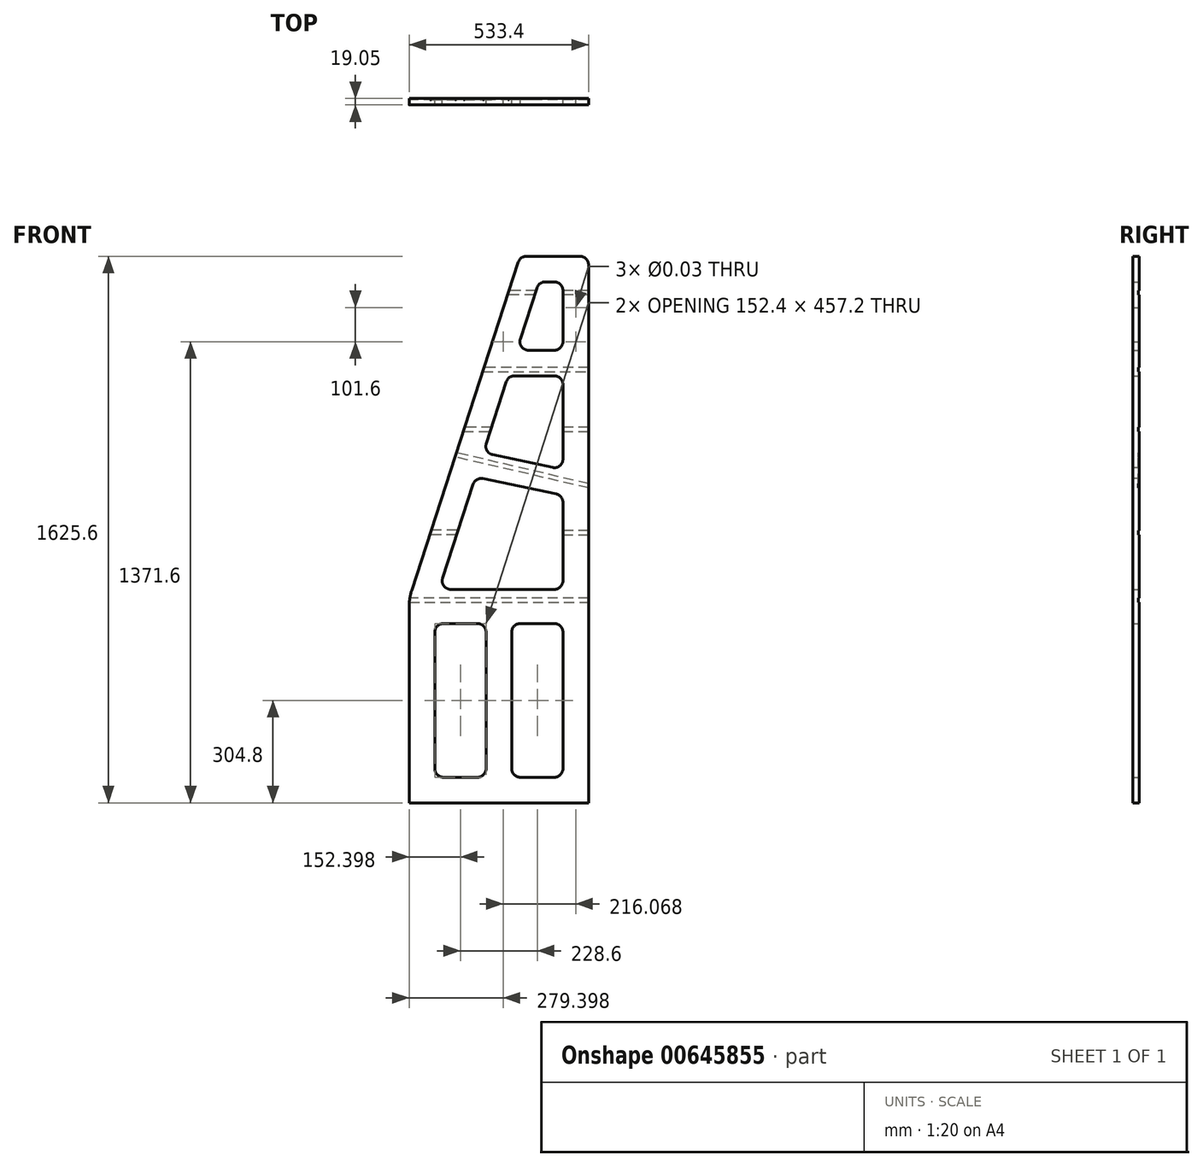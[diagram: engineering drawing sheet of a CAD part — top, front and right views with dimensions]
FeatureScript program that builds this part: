
annotation { "Feature Type Name" : "Feature", "Feature Type Description" : "" }
export const myFeature = defineFeature(function(context is Context, id is Id, definition is map)
    precondition{}
    {
        {
            var Q0;
            Q0=qCreatedBy(makeId("Front.planeOp"),FACE);
            var sketch = newSketch(context, id + "F0", { "sketchPlane" : qUnion([Q0])});
            skLineSegment(sketch, "E0.bottom", {"start": v(223.33, 799.48) * mm, "end": v(20.13, 799.48) * mm});
            skLineSegment(sketch, "E0.top", {"start": v(223.33, -826.12) * mm, "end": v(-310.07, -826.12) * mm});
            skLineSegment(sketch, "E0.left", {"start": v(223.33, 799.48) * mm, "end": v(223.33, -826.12) * mm});
            skLineSegment(sketch, "E0.right", {"start": v(-310.07, -216.52) * mm, "end": v(-310.07, -826.12) * mm});
            skPoint(sketch, "E0.middle", {"position": v(-43.37, -13.32) * mm});
            skLineSegment(sketch, "E1", {"start": v(-310.07, -216.52) * mm, "end": v(20.13, 799.48) * mm});
            skPoint(sketch, "E2.orphan", {"position": v(-310.07, 799.48) * mm});
            skPoint(sketch, "E3", {"position": v(-233.87, -749.92) * mm});
            skPoint(sketch, "E4", {"position": v(147.13, -749.92) * mm});
            skPoint(sketch, "E5", {"position": v(147.13, -292.72) * mm});
            skPoint(sketch, "E6", {"position": v(-5.27, -292.72) * mm});
            skPoint(sketch, "E7", {"position": v(-5.27, -749.92) * mm});
            skPoint(sketch, "E8", {"position": v(-81.47, -292.72) * mm});
            skPoint(sketch, "E9", {"position": v(-81.47, -749.92) * mm});
            skPoint(sketch, "E10", {"position": v(-233.87, -292.72) * mm});
            skPoint(sketch, "E11", {"position": v(-221.7, -191.12) * mm});
            skPoint(sketch, "E12", {"position": v(147.13, -191.12) * mm});
            skPoint(sketch, "E13", {"position": v(147.13, 113.68) * mm});
            skPoint(sketch, "E14", {"position": v(-122.63, 113.68) * mm});
            skPoint(sketch, "E15", {"position": v(147.13, 215.28) * mm});
            skPoint(sketch, "E16", {"position": v(147.13, 723.28) * mm});
            skPoint(sketch, "E17", {"position": v(147.13, 443.88) * mm});
            skLineSegment(sketch, "E18", {"start": v(-233.87, -292.72) * mm, "end": v(-81.47, -292.72) * mm});
            skLineSegment(sketch, "E19", {"start": v(-81.47, -749.92) * mm, "end": v(-233.87, -749.92) * mm});
            skLineSegment(sketch, "E20", {"start": v(-233.87, -292.72) * mm, "end": v(-233.87, -749.92) * mm});
            skLineSegment(sketch, "E21", {"start": v(-81.47, -749.92) * mm, "end": v(-81.47, -292.72) * mm});
            skLineSegment(sketch, "E22", {"start": v(-5.27, -292.72) * mm, "end": v(-5.27, -749.92) * mm});
            skLineSegment(sketch, "E23", {"start": v(-5.27, -749.92) * mm, "end": v(147.13, -749.92) * mm});
            skLineSegment(sketch, "E24", {"start": v(147.13, -749.92) * mm, "end": v(147.13, -292.72) * mm});
            skLineSegment(sketch, "E25", {"start": v(-5.27, -292.72) * mm, "end": v(147.13, -292.72) * mm});
            skLineSegment(sketch, "E26", {"start": v(-221.7, -191.12) * mm, "end": v(-122.63, 113.68) * mm});
            skLineSegment(sketch, "E27", {"start": v(-221.7, -191.12) * mm, "end": v(147.13, -191.12) * mm});
            skLineSegment(sketch, "E28", {"start": v(147.13, -191.12) * mm, "end": v(147.13, 113.68) * mm});
            skPoint(sketch, "E29", {"position": v(-89.61, 215.28) * mm});
            skLineSegment(sketch, "E30", {"start": v(147.13, 215.28) * mm, "end": v(147.13, 443.88) * mm});
            skPoint(sketch, "E31", {"position": v(-15.32, 443.88) * mm});
            skPoint(sketch, "E32", {"position": v(147.13, 520.08) * mm});
            skPoint(sketch, "E33", {"position": v(9.45, 520.08) * mm});
            skLineSegment(sketch, "E34", {"start": v(-15.32, 443.88) * mm, "end": v(147.13, 443.88) * mm});
            skLineSegment(sketch, "E35", {"start": v(-15.32, 443.88) * mm, "end": v(-89.61, 215.28) * mm});
            skLineSegment(sketch, "E36", {"start": v(147.13, 723.28) * mm, "end": v(147.13, 520.08) * mm});
            skLineSegment(sketch, "E37", {"start": v(147.13, 520.08) * mm, "end": v(9.45, 520.08) * mm});
            skLineSegment(sketch, "E38", {"start": v(147.13, 723.28) * mm, "end": v(75.3, 723.28) * mm});
            skLineSegment(sketch, "E39", {"start": v(9.45, 520.08) * mm, "end": v(75.3, 723.28) * mm});
            skPoint(sketch, "E40", {"position": v(147.13, 88.28) * mm});
            skPoint(sketch, "E41", {"position": v(147.13, 164.48) * mm});
            skLineSegment(sketch, "E42", {"start": v(-89.61, 215.28) * mm, "end": v(147.13, 164.48) * mm});
            skLineSegment(sketch, "E43", {"start": v(147.13, 164.48) * mm, "end": v(147.13, 215.28) * mm});
            skPoint(sketch, "E44", {"position": v(-113.17, 142.81) * mm});
            skLineSegment(sketch, "E45", {"start": v(-113.17, 142.81) * mm, "end": v(147.13, 88.28) * mm});
            skLineSegment(sketch, "E46", {"start": v(-122.63, 113.68) * mm, "end": v(-113.17, 142.81) * mm});
            skSolve(sketch);
        }
        {
            var Q0;
            Q0=makeQuery(id+"F0.imprint","IMPRINT",FACE,{"disambiguationData":[TD([[makeQuery(id+"F0.imprint","IMPRINT",EDGE,{"derivedFrom":sQuery(id+"F0.wireOp",EDGE,"E0.bottom")}),1.0]])]});
            extrude(context, id + "F1", {"entities" : qUnion([Q0]), "depth" : 19.05 * mm, "offsetDistance" : 25 * mm});
        }
        {
            var Q0;
            Q0=makeQuery(id+"F1.opExtrude","SWEPT_EDGE",EDGE,{"disambiguationData":[OSD([sQuery(id+"F0.wireOp",EDGE,"E19"),sQuery(id+"F0.wireOp",EDGE,"E20")])]});
            var Q1;
            Q1=makeQuery(id+"F1.opExtrude","SWEPT_EDGE",EDGE,{"disambiguationData":[OSD([sQuery(id+"F0.wireOp",EDGE,"E26"),sQuery(id+"F0.wireOp",EDGE,"E27")])]});
            var Q2;
            Q2=makeQuery(id+"F1.opExtrude","SWEPT_EDGE",EDGE,{"disambiguationData":[OSD([sQuery(id+"F0.wireOp",EDGE,"E35"),sQuery(id+"F0.wireOp",EDGE,"E42")])]});
            var Q3;
            Q3=makeQuery(id+"F1.opExtrude","SWEPT_EDGE",EDGE,{"disambiguationData":[OSD([sQuery(id+"F0.wireOp",EDGE,"E37"),sQuery(id+"F0.wireOp",EDGE,"E39")])]});
            var Q4;
            Q4=makeQuery(id+"F1.opExtrude","SWEPT_EDGE",EDGE,{"disambiguationData":[OSD([sQuery(id+"F0.wireOp",EDGE,"E36"),sQuery(id+"F0.wireOp",EDGE,"E37")])]});
            var Q5;
            Q5=makeQuery(id+"F1.opExtrude","SWEPT_EDGE",EDGE,{"disambiguationData":[OSD([sQuery(id+"F0.wireOp",EDGE,"E42"),sQuery(id+"F0.wireOp",EDGE,"E43")])]});
            var Q6;
            Q6=makeQuery(id+"F1.opExtrude","SWEPT_EDGE",EDGE,{"disambiguationData":[OSD([sQuery(id+"F0.wireOp",EDGE,"E27"),sQuery(id+"F0.wireOp",EDGE,"E28")])]});
            var Q7;
            Q7=makeQuery(id+"F1.opExtrude","SWEPT_EDGE",EDGE,{"disambiguationData":[OSD([sQuery(id+"F0.wireOp",EDGE,"E23"),sQuery(id+"F0.wireOp",EDGE,"E24")])]});
            var Q8;
            Q8=makeQuery(id+"F1.opExtrude","SWEPT_EDGE",EDGE,{"disambiguationData":[OSD([sQuery(id+"F0.wireOp",EDGE,"E19"),sQuery(id+"F0.wireOp",EDGE,"E21")])]});
            var Q9;
            Q9=makeQuery(id+"F1.opExtrude","SWEPT_EDGE",EDGE,{"disambiguationData":[OSD([sQuery(id+"F0.wireOp",EDGE,"E22"),sQuery(id+"F0.wireOp",EDGE,"E23")])]});
            var Q10;
            Q10=makeQuery(id+"F1.opExtrude","SWEPT_EDGE",EDGE,{"disambiguationData":[OSD([sQuery(id+"F0.wireOp",EDGE,"E24"),sQuery(id+"F0.wireOp",EDGE,"E25")])]});
            var Q11;
            Q11=makeQuery(id+"F1.opExtrude","SWEPT_EDGE",EDGE,{"disambiguationData":[OSD([sQuery(id+"F0.wireOp",EDGE,"E22"),sQuery(id+"F0.wireOp",EDGE,"E25")])]});
            var Q12;
            Q12=makeQuery(id+"F1.opExtrude","SWEPT_EDGE",EDGE,{"disambiguationData":[OSD([sQuery(id+"F0.wireOp",EDGE,"E18"),sQuery(id+"F0.wireOp",EDGE,"E20")])]});
            var Q13;
            Q13=makeQuery(id+"F1.opExtrude","SWEPT_EDGE",EDGE,{"disambiguationData":[OSD([sQuery(id+"F0.wireOp",EDGE,"E18"),sQuery(id+"F0.wireOp",EDGE,"E21")])]});
            var Q14;
            Q14=makeQuery(id+"F1.opExtrude","SWEPT_EDGE",EDGE,{"disambiguationData":[OSD([sQuery(id+"F0.wireOp",EDGE,"E28"),sQuery(id+"F0.wireOp",EDGE,"E45")])]});
            var Q15;
            Q15=makeQuery(id+"F1.opExtrude","SWEPT_EDGE",EDGE,{"disambiguationData":[OSD([sQuery(id+"F0.wireOp",EDGE,"E30"),sQuery(id+"F0.wireOp",EDGE,"E34")])]});
            var Q16;
            Q16=makeQuery(id+"F1.opExtrude","SWEPT_EDGE",EDGE,{"disambiguationData":[OSD([sQuery(id+"F0.wireOp",EDGE,"E36"),sQuery(id+"F0.wireOp",EDGE,"E38")])]});
            var Q17;
            Q17=makeQuery(id+"F1.opExtrude","SWEPT_EDGE",EDGE,{"disambiguationData":[OSD([sQuery(id+"F0.wireOp",EDGE,"E34"),sQuery(id+"F0.wireOp",EDGE,"E35")])]});
            var Q18;
            Q18=makeQuery(id+"F1.opExtrude","SWEPT_EDGE",EDGE,{"disambiguationData":[OSD([sQuery(id+"F0.wireOp",EDGE,"E38"),sQuery(id+"F0.wireOp",EDGE,"E39")])]});
            var Q19;
            Q19=makeQuery(id+"F1.opExtrude","SWEPT_EDGE",EDGE,{"disambiguationData":[OSD([sQuery(id+"F0.wireOp",EDGE,"E45"),sQuery(id+"F0.wireOp",EDGE,"E46")])]});
            var Q20;
            Q20=makeQuery(id+"F1.opExtrude","SWEPT_EDGE",EDGE,{"disambiguationData":[OSD([sQuery(id+"F0.wireOp",EDGE,"E0.bottom"),sQuery(id+"F0.wireOp",EDGE,"E0.left")])]});
            var Q21;
            Q21=makeQuery(id+"F1.opExtrude","SWEPT_EDGE",EDGE,{"disambiguationData":[OSD([sQuery(id+"F0.wireOp",EDGE,"E0.bottom"),sQuery(id+"F0.wireOp",EDGE,"E1")])]});
            fillet(context, id + "F2", {"entities" : qUnion([Q0, Q1, Q2, Q3, Q4, Q5, Q6, Q7, Q8, Q9, Q10, Q11, Q12, Q13, Q14, Q15, Q16, Q17, Q18, Q19, Q20, Q21]), "radius" : 25.4 * mm, "tangentPropagation" : true, "allowEdgeOverflow" : false});
        }
        {
            var Q0;
            Q0=makeQuery(id+"F1.opExtrude","SWEPT_EDGE",EDGE,{"disambiguationData":[OSD([sQuery(id+"F0.wireOp",EDGE,"E0.right"),sQuery(id+"F0.wireOp",EDGE,"E1")])]});
            fillet(context, id + "F3", {"entities" : qUnion([Q0]), "radius" : 152.4 * mm, "tangentPropagation" : true, "allowEdgeOverflow" : false});
        }
        {
            var Q0;
            Q0=makeQuery(id+"F1.opExtrude","CAP_FACE",FACE,{"disambiguationData":[OSD([sQuery(id+"F0.wireOp",EDGE,"E0.bottom"),sQuery(id+"F0.wireOp",EDGE,"E0.top"),sQuery(id+"F0.wireOp",EDGE,"E0.left"),sQuery(id+"F0.wireOp",EDGE,"E0.right"),sQuery(id+"F0.wireOp",EDGE,"E1"),sQuery(id+"F0.wireOp",EDGE,"E18"),sQuery(id+"F0.wireOp",EDGE,"E19"),sQuery(id+"F0.wireOp",EDGE,"E20"),sQuery(id+"F0.wireOp",EDGE,"E21"),sQuery(id+"F0.wireOp",EDGE,"E22"),sQuery(id+"F0.wireOp",EDGE,"E23"),sQuery(id+"F0.wireOp",EDGE,"E24"),sQuery(id+"F0.wireOp",EDGE,"E25"),sQuery(id+"F0.wireOp",EDGE,"E26"),sQuery(id+"F0.wireOp",EDGE,"E27"),sQuery(id+"F0.wireOp",EDGE,"E28"),sQuery(id+"F0.wireOp",EDGE,"E30"),sQuery(id+"F0.wireOp",EDGE,"E34"),sQuery(id+"F0.wireOp",EDGE,"E35"),sQuery(id+"F0.wireOp",EDGE,"E36"),sQuery(id+"F0.wireOp",EDGE,"E37"),sQuery(id+"F0.wireOp",EDGE,"E38"),sQuery(id+"F0.wireOp",EDGE,"E39"),sQuery(id+"F0.wireOp",EDGE,"E42"),sQuery(id+"F0.wireOp",EDGE,"E43"),sQuery(id+"F0.wireOp",EDGE,"E45"),sQuery(id+"F0.wireOp",EDGE,"E46")])],"isStart":true});
            var sketch = newSketch(context, id + "F4", { "sketchPlane" : qUnion([Q0])});
            skPoint(sketch, "E47", {"position": v(169.74, 215.28) * mm});
            skPoint(sketch, "E48", {"position": v(-223.33, 123.2) * mm});
            skPoint(sketch, "E49", {"position": v(173.86, 202.58) * mm});
            skPoint(sketch, "E50", {"position": v(-223.33, 110.5) * mm});
            skLineSegment(sketch, "E51", {"start": v(-223.33, 123.2) * mm, "end": v(169.74, 215.28) * mm});
            skLineSegment(sketch, "E52", {"start": v(-223.33, 110.5) * mm, "end": v(173.86, 202.58) * mm});
            skLineSegment(sketch, "E53", {"start": v(-223.33, 123.2) * mm, "end": v(-223.33, 110.5) * mm});
            skLineSegment(sketch, "E54", {"start": v(169.74, 215.28) * mm, "end": v(173.86, 202.58) * mm});
            skSolve(sketch);
        }
        {
            var Q0;
            Q0=makeQuery(id+"F4.imprint","IMPRINT",FACE,{"disambiguationData":[TD([[makeQuery(id+"F4.imprint","IMPRINT",EDGE,{"derivedFrom":sQuery(id+"F4.wireOp",EDGE,"E51")}),-1.0]])]});
            extrude(context, id + "F5", {"entities" : qUnion([Q0]), "operationType" : NewBodyOperationType.REMOVE, "oppositeDirection" : true, "depth" : 3.17 * mm, "offsetDistance" : 25.4 * mm});
        }
        {
            var Q0;
            {var subQ0=sQuery(id+"F0.wireOp",EDGE,"E28");var subQ1=sQuery(id+"F0.wireOp",EDGE,"E23");var subQ2=sQuery(id+"F0.wireOp",EDGE,"E22");var subQ3=sQuery(id+"F0.wireOp",EDGE,"E27");var subQ4=sQuery(id+"F0.wireOp",EDGE,"E25");var subQ5=sQuery(id+"F0.wireOp",EDGE,"E46");var subQ6=sQuery(id+"F0.wireOp",EDGE,"E26");var subQ7=sQuery(id+"F0.wireOp",EDGE,"E20");var subQ8=sQuery(id+"F0.wireOp",EDGE,"E19");var subQ9=sQuery(id+"F0.wireOp",EDGE,"E21");var subQ10=sQuery(id+"F0.wireOp",EDGE,"E24");var subQ11=sQuery(id+"F0.wireOp",EDGE,"E1");var subQ12=sQuery(id+"F0.wireOp",EDGE,"E0.right");var subQ13=sQuery(id+"F0.wireOp",EDGE,"E0.left");var subQ14=sQuery(id+"F0.wireOp",EDGE,"E45");var subQ15=sQuery(id+"F0.wireOp",EDGE,"E0.top");var subQ16=sQuery(id+"F0.wireOp",EDGE,"E18");Q0=makeQuery(id+"F5.boolean.opBoolean","SPLIT",FACE,{"disambiguationData":[TD([makeQuery(id+"F1.opExtrude","SWEPT_FACE",FACE,{"disambiguationData":[OSD([subQ15])]})])],"derivedFrom":makeQuery(id+"F1.opExtrude","CAP_FACE",FACE,{"disambiguationData":[OSD([sQuery(id+"F0.wireOp",EDGE,"E0.bottom"),subQ15,subQ13,subQ12,subQ11,subQ16,subQ8,subQ7,subQ9,subQ2,subQ1,subQ10,subQ4,subQ6,subQ3,subQ0,sQuery(id+"F0.wireOp",EDGE,"E30"),sQuery(id+"F0.wireOp",EDGE,"E34"),sQuery(id+"F0.wireOp",EDGE,"E35"),sQuery(id+"F0.wireOp",EDGE,"E36"),sQuery(id+"F0.wireOp",EDGE,"E37"),sQuery(id+"F0.wireOp",EDGE,"E38"),sQuery(id+"F0.wireOp",EDGE,"E39"),sQuery(id+"F0.wireOp",EDGE,"E42"),sQuery(id+"F0.wireOp",EDGE,"E43"),subQ14,subQ5])],"isStart":true})});}
            var sketch = newSketch(context, id + "F6", { "sketchPlane" : qUnion([Q0])});
            skPoint(sketch, "E55", {"position": v(-223.33, -16.5) * mm});
            skPoint(sketch, "E56", {"position": v(-223.33, -29.2) * mm});
            skLineSegment(sketch, "E57", {"start": v(-223.33, -16.5) * mm, "end": v(-147.13, -16.5) * mm});
            skLineSegment(sketch, "E58", {"start": v(-147.13, -16.5) * mm, "end": v(-147.13, -29.2) * mm});
            skLineSegment(sketch, "E59", {"start": v(-147.13, -29.2) * mm, "end": v(-223.33, -29.2) * mm});
            skSolve(sketch);
        }
        {
            var Q0;
            Q0 = qSketchRegion(id + "F6", true);
            var Q1;
            {var subQ0=sQuery(id+"F6.wireOp",EDGE,"E57");Q1=makeQuery(id+"F6.imprint","IMPRINT",FACE,{"disambiguationData":[TD([[makeQuery(id+"F6.imprint","IMPRINT",EDGE,{"derivedFrom":subQ0}),-1.0]])]});}
            extrude(context, id + "F7", {"entities" : qUnion([Q0, Q1]), "operationType" : NewBodyOperationType.REMOVE, "oppositeDirection" : true, "depth" : 3.17 * mm, "offsetDistance" : 25.4 * mm});
        }
        {
            var Q0;
            {var subQ0=sQuery(id+"F0.wireOp",EDGE,"E39");var subQ1=sQuery(id+"F0.wireOp",EDGE,"E38");var subQ2=sQuery(id+"F0.wireOp",EDGE,"E36");var subQ3=sQuery(id+"F0.wireOp",EDGE,"E0.bottom");var subQ4=sQuery(id+"F0.wireOp",EDGE,"E42");var subQ5=sQuery(id+"F0.wireOp",EDGE,"E35");var subQ6=sQuery(id+"F0.wireOp",EDGE,"E34");var subQ7=sQuery(id+"F0.wireOp",EDGE,"E30");var subQ8=sQuery(id+"F0.wireOp",EDGE,"E37");var subQ9=sQuery(id+"F0.wireOp",EDGE,"E0.left");var subQ10=sQuery(id+"F0.wireOp",EDGE,"E1");var subQ11=sQuery(id+"F0.wireOp",EDGE,"E43");Q0=makeQuery(id+"F5.boolean.opBoolean","SPLIT",FACE,{"disambiguationData":[TD([makeQuery(id+"F1.opExtrude","SWEPT_FACE",FACE,{"disambiguationData":[OSD([subQ3])]})])],"derivedFrom":makeQuery(id+"F1.opExtrude","CAP_FACE",FACE,{"disambiguationData":[OSD([subQ3,sQuery(id+"F0.wireOp",EDGE,"E0.top"),subQ9,sQuery(id+"F0.wireOp",EDGE,"E0.right"),subQ10,sQuery(id+"F0.wireOp",EDGE,"E18"),sQuery(id+"F0.wireOp",EDGE,"E19"),sQuery(id+"F0.wireOp",EDGE,"E20"),sQuery(id+"F0.wireOp",EDGE,"E21"),sQuery(id+"F0.wireOp",EDGE,"E22"),sQuery(id+"F0.wireOp",EDGE,"E23"),sQuery(id+"F0.wireOp",EDGE,"E24"),sQuery(id+"F0.wireOp",EDGE,"E25"),sQuery(id+"F0.wireOp",EDGE,"E26"),sQuery(id+"F0.wireOp",EDGE,"E27"),sQuery(id+"F0.wireOp",EDGE,"E28"),subQ7,subQ6,subQ5,subQ2,subQ8,subQ1,subQ0,subQ4,subQ11,sQuery(id+"F0.wireOp",EDGE,"E45"),sQuery(id+"F0.wireOp",EDGE,"E46")])],"isStart":true})});}
            var sketch = newSketch(context, id + "F8", { "sketchPlane" : qUnion([Q0])});
            skPoint(sketch, "E60", {"position": v(-223.33, 685.18) * mm});
            skPoint(sketch, "E61", {"position": v(-223.33, 697.88) * mm});
            skLineSegment(sketch, "E62", {"start": v(-223.33, 697.88) * mm, "end": v(12.9, 697.88) * mm});
            skLineSegment(sketch, "E63", {"start": v(-223.33, 685.18) * mm, "end": v(-223.33, 697.88) * mm});
            skLineSegment(sketch, "E64", {"start": v(-223.33, 685.18) * mm, "end": v(50.2, 685.18) * mm});
            skLineSegment(sketch, "E65", {"start": v(50.2, 685.18) * mm, "end": v(12.9, 697.88) * mm});
            skSolve(sketch);
        }
        {
            var Q0;
            {var subQ8=sQuery(id+"F8.wireOp",EDGE,"E63");Q0=makeQuery(id+"F8.imprint","IMPRINT",FACE,{"disambiguationData":[TD([[makeQuery(id+"F8.imprint","IMPRINT",EDGE,{"derivedFrom":subQ8}),1.0]])]});}
            var Q1;
            {var subQ0=sQuery(id+"F8.wireOp",EDGE,"gvT0msbo-aJb6-UwI5-asTA-rgO9hPE7J7Gs");Q1=makeQuery(id+"F8.imprint","IMPRINT",FACE,{"disambiguationData":[TD([[makeQuery(id+"F8.imprint","IMPRINT",EDGE,{"derivedFrom":subQ0}),1.0]])]});}
            extrude(context, id + "F9", {"entities" : qUnion([Q0, Q1]), "operationType" : NewBodyOperationType.REMOVE, "oppositeDirection" : true, "depth" : 3.17 * mm, "offsetDistance" : 25.4 * mm});
        }
        {
            var Q0;
            {var subQ0=sQuery(id+"F0.wireOp",EDGE,"E39");var subQ1=sQuery(id+"F0.wireOp",EDGE,"E38");var subQ2=sQuery(id+"F0.wireOp",EDGE,"E36");var subQ3=sQuery(id+"F0.wireOp",EDGE,"E0.bottom");var subQ4=sQuery(id+"F0.wireOp",EDGE,"E42");var subQ5=sQuery(id+"F0.wireOp",EDGE,"E35");var subQ6=sQuery(id+"F0.wireOp",EDGE,"E34");var subQ7=sQuery(id+"F0.wireOp",EDGE,"E30");var subQ8=sQuery(id+"F0.wireOp",EDGE,"E37");var subQ9=sQuery(id+"F0.wireOp",EDGE,"E0.left");var subQ10=sQuery(id+"F0.wireOp",EDGE,"E1");var subQ11=sQuery(id+"F0.wireOp",EDGE,"E43");Q0=makeQuery(id+"F5.boolean.opBoolean","SPLIT",FACE,{"disambiguationData":[TD([makeQuery(id+"F1.opExtrude","SWEPT_FACE",FACE,{"disambiguationData":[OSD([subQ3])]})])],"derivedFrom":makeQuery(id+"F1.opExtrude","CAP_FACE",FACE,{"disambiguationData":[OSD([subQ3,sQuery(id+"F0.wireOp",EDGE,"E0.top"),subQ9,sQuery(id+"F0.wireOp",EDGE,"E0.right"),subQ10,sQuery(id+"F0.wireOp",EDGE,"E18"),sQuery(id+"F0.wireOp",EDGE,"E19"),sQuery(id+"F0.wireOp",EDGE,"E20"),sQuery(id+"F0.wireOp",EDGE,"E21"),sQuery(id+"F0.wireOp",EDGE,"E22"),sQuery(id+"F0.wireOp",EDGE,"E23"),sQuery(id+"F0.wireOp",EDGE,"E24"),sQuery(id+"F0.wireOp",EDGE,"E25"),sQuery(id+"F0.wireOp",EDGE,"E26"),sQuery(id+"F0.wireOp",EDGE,"E27"),sQuery(id+"F0.wireOp",EDGE,"E28"),subQ7,subQ6,subQ5,subQ2,subQ8,subQ1,subQ0,subQ4,subQ11,sQuery(id+"F0.wireOp",EDGE,"E45"),sQuery(id+"F0.wireOp",EDGE,"E46")])],"isStart":true})});}
            var sketch = newSketch(context, id + "F10", { "sketchPlane" : qUnion([Q0])});
            skLineSegment(sketch, "E66", {"start": v(-171.29, 697.88) * mm, "end": v(12.9, 697.88) * mm});
            skLineSegment(sketch, "E67", {"start": v(12.9, 697.88) * mm, "end": v(16.04, 688.18) * mm});
            skLineSegment(sketch, "E68", {"start": v(16.04, 688.18) * mm, "end": v(17.02, 685.18) * mm});
            skLineSegment(sketch, "E69", {"start": v(17.02, 685.18) * mm, "end": v(-220.33, 685.18) * mm});
            skLineSegment(sketch, "E70", {"start": v(-220.33, 685.18) * mm, "end": v(-220.33, 697.88) * mm});
            skLineSegment(sketch, "E71", {"start": v(-220.33, 697.88) * mm, "end": v(-165.3, 697.88) * mm});
            skSolve(sketch);
        }
        {
            var Q0;
            {var subQ11=sQuery(id+"F10.wireOp",EDGE,"E70");Q0=makeQuery(id+"F10.imprint","IMPRINT",FACE,{"disambiguationData":[TD([[makeQuery(id+"F10.imprint","IMPRINT",EDGE,{"derivedFrom":subQ11}),-1.0]])]});}
            var Q1;
            {var subQ5=sQuery(id+"F10.wireOp",EDGE,"E67");Q1=makeQuery(id+"F10.imprint","IMPRINT",FACE,{"disambiguationData":[TD([[makeQuery(id+"F10.imprint","IMPRINT",EDGE,{"derivedFrom":subQ5}),1.0]])]});}
            extrude(context, id + "F11", {"entities" : qUnion([Q0, Q1]), "operationType" : NewBodyOperationType.REMOVE, "oppositeDirection" : true, "depth" : 3.17 * mm, "offsetDistance" : 25.4 * mm});
        }
        {
            var Q0;
            {var subQ0=sQuery(id+"F0.wireOp",EDGE,"E34");var subQ1=sQuery(id+"F0.wireOp",EDGE,"E30");var subQ3=sQuery(id+"F0.wireOp",EDGE,"E36");var subQ5=sQuery(id+"F0.wireOp",EDGE,"E42");var subQ7=sQuery(id+"F0.wireOp",EDGE,"E37");var subQ9=sQuery(id+"F0.wireOp",EDGE,"E39");var subQ12=sQuery(id+"F0.wireOp",EDGE,"E35");var subQ15=sQuery(id+"F0.wireOp",EDGE,"E0.left");var subQ17=makeQuery(id+"F1.opExtrude","SWEPT_FACE",FACE,{"disambiguationData":[OSD([subQ0])]});var subQ18=sQuery(id+"F0.wireOp",EDGE,"E1");var subQ20=sQuery(id+"F0.wireOp",EDGE,"E43");var subQ26=sQuery(id+"F0.wireOp",EDGE,"E38");var subQ27=sQuery(id+"F0.wireOp",EDGE,"E0.bottom");Q0=makeQuery(id+"F11.boolean.opBoolean","SPLIT",FACE,{"disambiguationData":[TD([subQ17])],"derivedFrom":makeQuery(id+"F5.boolean.opBoolean","SPLIT",FACE,{"disambiguationData":[TD([makeQuery(id+"F1.opExtrude","SWEPT_FACE",FACE,{"disambiguationData":[OSD([subQ27])]})])],"derivedFrom":makeQuery(id+"F1.opExtrude","CAP_FACE",FACE,{"disambiguationData":[OSD([subQ27,sQuery(id+"F0.wireOp",EDGE,"E0.top"),subQ15,sQuery(id+"F0.wireOp",EDGE,"E0.right"),subQ18,sQuery(id+"F0.wireOp",EDGE,"E18"),sQuery(id+"F0.wireOp",EDGE,"E19"),sQuery(id+"F0.wireOp",EDGE,"E20"),sQuery(id+"F0.wireOp",EDGE,"E21"),sQuery(id+"F0.wireOp",EDGE,"E22"),sQuery(id+"F0.wireOp",EDGE,"E23"),sQuery(id+"F0.wireOp",EDGE,"E24"),sQuery(id+"F0.wireOp",EDGE,"E25"),sQuery(id+"F0.wireOp",EDGE,"E26"),sQuery(id+"F0.wireOp",EDGE,"E27"),sQuery(id+"F0.wireOp",EDGE,"E28"),subQ1,subQ0,subQ12,subQ3,subQ7,subQ26,subQ9,subQ5,subQ20,sQuery(id+"F0.wireOp",EDGE,"E45"),sQuery(id+"F0.wireOp",EDGE,"E46")])],"isStart":true})})});}
            var sketch = newSketch(context, id + "F12", { "sketchPlane" : qUnion([Q0])});
            skPoint(sketch, "E72", {"position": v(-223.33, 469.28) * mm});
            skPoint(sketch, "E73", {"position": v(-223.33, 456.58) * mm});
            skPoint(sketch, "E74", {"position": v(-223.33, 291.48) * mm});
            skPoint(sketch, "E75", {"position": v(-223.33, 278.78) * mm});
            skLineSegment(sketch, "E76", {"start": v(-223.33, 469.28) * mm, "end": v(87.19, 469.28) * mm});
            skLineSegment(sketch, "E77", {"start": v(87.19, 469.28) * mm, "end": v(91.31, 456.58) * mm});
            skLineSegment(sketch, "E78", {"start": v(91.31, 456.58) * mm, "end": v(-223.33, 456.58) * mm});
            skLineSegment(sketch, "E79", {"start": v(-223.33, 469.28) * mm, "end": v(-223.33, 456.58) * mm});
            skLineSegment(sketch, "E80", {"start": v(-223.33, 291.48) * mm, "end": v(144.97, 291.48) * mm});
            skLineSegment(sketch, "E81", {"start": v(144.97, 291.48) * mm, "end": v(169.74, 278.78) * mm});
            skLineSegment(sketch, "E82", {"start": v(169.74, 278.78) * mm, "end": v(-223.33, 278.78) * mm});
            skLineSegment(sketch, "E83", {"start": v(-223.33, 291.48) * mm, "end": v(-223.33, 278.78) * mm});
            skPoint(sketch, "E84", {"position": v(-185.4, 647.08) * mm});
            skPoint(sketch, "E85", {"position": v(-185.4, 545.48) * mm});
            skSolve(sketch);
        }
        {
            var Q0;
            Q0 = qSketchRegion(id + "F12", true);
            extrude(context, id + "F13", {"entities" : qUnion([Q0]), "operationType" : NewBodyOperationType.REMOVE, "oppositeDirection" : true, "depth" : 3.17 * mm, "offsetDistance" : 25.4 * mm});
        }
        {
            var Q0;
            Q0=sQuery(id+"F12.wireOp",VERTEX,"E84");
            var Q1;
            Q1=sQuery(id+"F12.wireOp",VERTEX,"E85");
            var Q2;
            Q2=makeQuery(id+"F1.opExtrude","SWEPT_BODY",BODY,{"disambiguationData":[OSD([sQuery(id+"F0.wireOp",EDGE,"E0.bottom"),sQuery(id+"F0.wireOp",EDGE,"E0.top"),sQuery(id+"F0.wireOp",EDGE,"E0.left"),sQuery(id+"F0.wireOp",EDGE,"E0.right"),sQuery(id+"F0.wireOp",EDGE,"E1"),sQuery(id+"F0.wireOp",EDGE,"E18"),sQuery(id+"F0.wireOp",EDGE,"E19"),sQuery(id+"F0.wireOp",EDGE,"E20"),sQuery(id+"F0.wireOp",EDGE,"E21"),sQuery(id+"F0.wireOp",EDGE,"E22"),sQuery(id+"F0.wireOp",EDGE,"E23"),sQuery(id+"F0.wireOp",EDGE,"E24"),sQuery(id+"F0.wireOp",EDGE,"E25"),sQuery(id+"F0.wireOp",EDGE,"E26"),sQuery(id+"F0.wireOp",EDGE,"E27"),sQuery(id+"F0.wireOp",EDGE,"E28"),sQuery(id+"F0.wireOp",EDGE,"E30"),sQuery(id+"F0.wireOp",EDGE,"E34"),sQuery(id+"F0.wireOp",EDGE,"E35"),sQuery(id+"F0.wireOp",EDGE,"E36"),sQuery(id+"F0.wireOp",EDGE,"E37"),sQuery(id+"F0.wireOp",EDGE,"E38"),sQuery(id+"F0.wireOp",EDGE,"E39"),sQuery(id+"F0.wireOp",EDGE,"E42"),sQuery(id+"F0.wireOp",EDGE,"E43"),sQuery(id+"F0.wireOp",EDGE,"E45"),sQuery(id+"F0.wireOp",EDGE,"E46")])]});
            hole(context, id + "F14", {"style" : HoleStyle.SIMPLE, "endStyle" : HoleEndStyle.THROUGH, "standardTappedOrClearance" : lookupTablePath({ "standard" : "ANSI", "size" : "3/4 (0.75)", "type" : "Drilled" }), "standardBlindInLast" : lookupTablePath({ "standard" : "ANSI", "size" : "3/4", "type" : "Drilled" }), "holeDiameter" : 3 / 101.6 * mm, "majorDiameter" : 8 * mm, "isTappedThrough" : true, "tappedDepth" : 12.7 * mm, "tapClearance" : 3, "startFromSketch" : true, "locations" : qUnion([Q0, Q1]), "scope" : qUnion([Q2])});
        }
        {
            var Q0;
            {var subQ7=sQuery(id+"F12.wireOp",EDGE,"E76");Q0=makeQuery(id+"F12.imprint","IMPRINT",FACE,{"disambiguationData":[TD([[makeQuery(id+"F12.imprint","IMPRINT",EDGE,{"derivedFrom":subQ7}),1.0]])]});}
            var sketch = newSketch(context, id + "F15", { "sketchPlane" : qUnion([Q0])});
            skPoint(sketch, "E86", {"position": v(30.67, 545.48) * mm});
            skLineSegment(sketch, "E87", {"start": v(-224.13, -28.53) * mm, "end": v(249.83, -28.53) * mm});
            skLineSegment(sketch, "E88", {"start": v(249.83, -13.11) * mm, "end": v(163.83, -13.11) * mm});
            skLineSegment(sketch, "E89", {"start": v(163.83, -13.11) * mm, "end": v(168.6, -28.53) * mm});
            skLineSegment(sketch, "E90", {"start": v(249.83, -28.53) * mm, "end": v(247.03, -13.11) * mm});
            skPoint(sketch, "E91", {"position": v(-227.67, -216.52) * mm});
            skPoint(sketch, "E92", {"position": v(-227.67, -229.22) * mm});
            skLineSegment(sketch, "E93", {"start": v(-227.67, -216.52) * mm, "end": v(313.08, -216.52) * mm});
            skLineSegment(sketch, "E94", {"start": v(313.08, -216.52) * mm, "end": v(313.08, -229.22) * mm});
            skLineSegment(sketch, "E95", {"start": v(313.08, -229.22) * mm, "end": v(-227.67, -229.22) * mm});
            skLineSegment(sketch, "E96", {"start": v(-227.67, -216.52) * mm, "end": v(-227.67, -229.22) * mm});
            skSolve(sketch);
        }
        {
            var Q0;
            Q0 = qSketchRegion(id + "F15", true);
            extrude(context, id + "F16", {"entities" : qUnion([Q0]), "operationType" : NewBodyOperationType.REMOVE, "oppositeDirection" : true, "depth" : 3.17 * mm, "offsetDistance" : 25.4 * mm});
        }
        {
            var Q0;
            Q0 = qSketchRegion(id + "F15", true);
            extrude(context, id + "F17", {"entities" : qUnion([Q0]), "operationType" : NewBodyOperationType.REMOVE, "oppositeDirection" : true, "depth" : 3.17 * mm, "offsetDistance" : 25.4 * mm});
        }
        {
            var Q0;
            Q0=sQuery(id+"F15.wireOp",VERTEX,"E86");
            var Q1;
            Q1=makeQuery(id+"F1.opExtrude","SWEPT_BODY",BODY,{"disambiguationData":[OSD([sQuery(id+"F0.wireOp",EDGE,"E0.bottom"),sQuery(id+"F0.wireOp",EDGE,"E0.top"),sQuery(id+"F0.wireOp",EDGE,"E0.left"),sQuery(id+"F0.wireOp",EDGE,"E0.right"),sQuery(id+"F0.wireOp",EDGE,"E1"),sQuery(id+"F0.wireOp",EDGE,"E18"),sQuery(id+"F0.wireOp",EDGE,"E19"),sQuery(id+"F0.wireOp",EDGE,"E20"),sQuery(id+"F0.wireOp",EDGE,"E21"),sQuery(id+"F0.wireOp",EDGE,"E22"),sQuery(id+"F0.wireOp",EDGE,"E23"),sQuery(id+"F0.wireOp",EDGE,"E24"),sQuery(id+"F0.wireOp",EDGE,"E25"),sQuery(id+"F0.wireOp",EDGE,"E26"),sQuery(id+"F0.wireOp",EDGE,"E27"),sQuery(id+"F0.wireOp",EDGE,"E28"),sQuery(id+"F0.wireOp",EDGE,"E30"),sQuery(id+"F0.wireOp",EDGE,"E34"),sQuery(id+"F0.wireOp",EDGE,"E35"),sQuery(id+"F0.wireOp",EDGE,"E36"),sQuery(id+"F0.wireOp",EDGE,"E37"),sQuery(id+"F0.wireOp",EDGE,"E38"),sQuery(id+"F0.wireOp",EDGE,"E39"),sQuery(id+"F0.wireOp",EDGE,"E42"),sQuery(id+"F0.wireOp",EDGE,"E43"),sQuery(id+"F0.wireOp",EDGE,"E45"),sQuery(id+"F0.wireOp",EDGE,"E46")])]});
            hole(context, id + "F18", {"style" : HoleStyle.SIMPLE, "endStyle" : HoleEndStyle.THROUGH, "standardTappedOrClearance" : lookupTablePath({ "standard" : "ANSI", "size" : "3/4 (0.75)", "type" : "Drilled" }), "standardBlindInLast" : lookupTablePath({ "standard" : "ANSI", "size" : "3/4", "type" : "Drilled" }), "holeDiameter" : 3 / 101.6 * mm, "majorDiameter" : 6.35 * mm, "isTappedThrough" : true, "tappedDepth" : 12.7 * mm, "tapClearance" : 3, "startFromSketch" : true, "locations" : qUnion([Q0]), "scope" : qUnion([Q1])});
        }
    });
